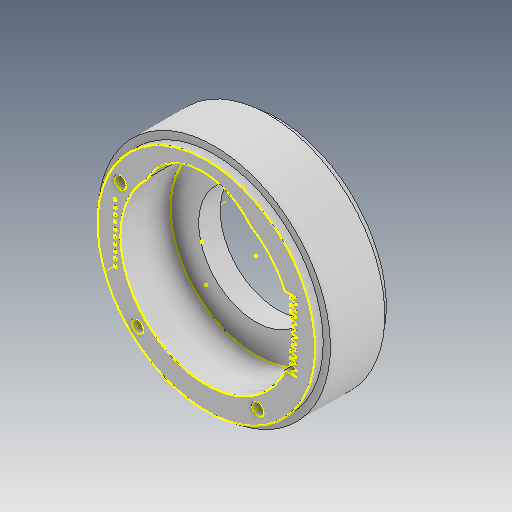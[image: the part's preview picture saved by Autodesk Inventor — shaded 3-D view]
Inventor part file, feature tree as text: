
AUTODESK INVENTOR PART (.ipt)
format: ipt  version: 2020.3 (Build 243373010, 373A)  size: 428,544 bytes
history: native  units: mm
features: sketch x15, extrude x14, projected_geometry x8, plane x3, pattern_linear x1, other x1
ambient origin geometry x8: Origin, YZ Plane, XZ Plane, XY Plane, X Axis, Y Axis, Z Axis, Center Point
bodies: Solid1 (feature_tree)
feature tree (42):
  extrude  "Extrusion1"  Depth=20.0mm
  extrude  "Extrusion2"  Depth=1.25mm
  extrude  "Extrusion3"  Depth=1.5mm
  extrude  "Extrusion4"  Depth=8.75mm TaperAngle=0.0deg
  extrude  "Extrusion5"  Depth=1.5mm TaperAngle=0.0deg
  plane  "Work Plane1"
  sketch  "Sketch7"  dims[d16=2.0mm d17=2.0mm]
  extrude  "Extrusion6"  Depth=2.0mm
  extrude  "Extrusion7"  Depth=15.0mm
  extrude  "Extrusion8"  Depth=9.0mm
  extrude  "Extrusion9"  Depth=8.0mm
  sketch  "Sketch11"  dims[d22=8.0mm d23=12.25mm]
  plane  "Work Plane2"
  plane  "Work Plane3"
  extrude  "Extrusion10"  Depth=5.5mm TaperAngle=0.0deg
  sketch  "Sketch13"  dims[d29=10.0mm d30=0.75mm d31=12.0mm d32=3.5mm d33=0.0mm]
  extrude  "Extrusion11"  Depth=0.75mm TaperAngle=0.0deg
  pattern_linear  "Rectangular Pattern1"  Count1=12 Spacing1=1.0mm
  other  "Work Axis1"
  extrude  "Extrusion12"  Depth=5.5mm TaperAngle=0.0deg
  sketch  "Sketch15"  dims[d34=4.363323mm]
  extrude  "Extrusion14"  Depth=10.75mm
  extrude  "Extrusion15"  Depth=5.0mm TaperAngle=0.0deg
  sketch  "Sketch20"  dims[d39=8.726646mm d40=120.0mm d42=1.0mm d43=10.0mm d45=10.0mm d47=2.5mm d48=0.0mm d49=10.75mm d50=5.0mm d51=0.0mm d53=15.0mm d54=7.5mm d55=1.5mm d56=5.0mm d57=0.0mm d58=0.0mm d59=-2.75mm d60=-20.0mm d61=3.5mm d62=3.0mm d63=5.0mm d64=0.035mm d65=0.0mm d66=7.0mm d67=0.0mm d68=7.0mm d69=0.0mm d70=0.415mm d71=15.85mm d72=5.0mm d73=5.0mm d74=0.0mm d75=15.0mm d76=2.5mm d77=100.0mm d79=10.0mm d80=13.0mm d81=0.75mm d82=0.75mm d83=0.25mm d84=0.75mm d85=0.0mm d88=5.0mm d89=0.0mm d90=12.25mm d91=12.25mm d92=14.25mm d93=9.0mm d94=12.0mm d95=15.0mm d96=8.0mm d97=5.5mm d98=0.0mm]
  sketch  "Sketch1"  dims[d0=40.45mm d2=20.0mm]
  sketch  "Sketch2"  dims[d3=12.5mm d4=0.0mm d6=1.25mm]
  projected_geometry  "Projected Loop1"
  sketch  "Sketch3"  dims[d7=1.5mm d8=0.0mm d9=40.45mm]
  sketch  "Sketch4"  dims[d10=30.0mm d11=8.75mm d12=0.0mm]
  sketch  "Sketch5"  dims[d13=1.25mm d14=1.5mm d15=0.0mm]
  sketch  "Sketch8"  dims[d18=2.0mm d19=15.0mm]
  sketch  "Sketch10"  dims[d20=12.0mm d21=9.0mm]
  projected_geometry  "Projected Loop3"
  sketch  "Sketch12"  dims[d24=14.25mm d25=5.5mm d26=0.0mm]
  projected_geometry  "Projected Loop4"
  sketch  "Sketch16"  dims[d36=1.0mm]
  projected_geometry  "Projected Loop5"
  projected_geometry  "Projected Loop6"
  sketch  "Sketch18"  dims[d38=0.075mm]
  projected_geometry  "Projected Loop9"
  projected_geometry  "Projected Loop10"
  projected_geometry  "Projected Loop12"
